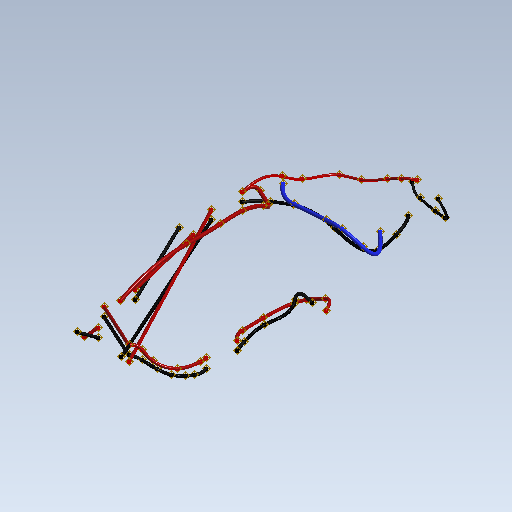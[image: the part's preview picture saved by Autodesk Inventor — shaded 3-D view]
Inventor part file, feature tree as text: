
AUTODESK INVENTOR PART (.ipt)
format: ipt  version: 2020.1 (Build 241239000, 239)  size: 1,614,336 bytes
history: native  units: mm (DEFAULTED — no unit token found)
features: other x136, plane x35, sketch x35, sweep x35
ambient origin geometry x8: Origin, YZ Plane, XZ Plane, XY Plane, X Axis, Y Axis, Z Axis, Center Point
bodies: Body1 (feature_tree), Body2 (feature_tree), Body3 (feature_tree), Body4 (feature_tree), Body5 (feature_tree), Body6 (feature_tree), Body7 (feature_tree), Body8 (feature_tree), Body9 (feature_tree), Body10 (feature_tree), Body11 (feature_tree), Body12 (feature_tree), Body13 (feature_tree), Body14 (feature_tree), Body15 (feature_tree), Body16 (feature_tree), Body17 (feature_tree), Body18 (feature_tree), Body19 (feature_tree), Body20 (feature_tree), Body21 (feature_tree), Body22 (feature_tree), Body23 (feature_tree), Body24 (feature_tree), Body25 (feature_tree), Body26 (feature_tree), Body27 (feature_tree), Body28 (feature_tree), Body29 (feature_tree), Body30 (feature_tree), Body31 (feature_tree), Body32 (feature_tree), Body33 (feature_tree), Body34 (feature_tree), Body35 (feature_tree)
feature tree (241):
  other  "Work Point1"
  other  "Work Point2"
  other  "P- / Switch>XT60"
  other  "Work Point3"
  other  "Work Point4"
  other  "P+ / Switch>XT60"
  other  "Work Point5"
  other  "Work Point6"
  other  "P- / XT60>XT60 VESC1"
  other  "Work Point7"
  other  "Work Point8"
  other  "P+ / XT60>XT60 VESC1"
  other  "Work Point9"
  other  "Work Point10"
  other  "P- / XT60>XT60 VESC2"
  other  "Work Point11"
  other  "Work Point12"
  other  "P+ / XT60>XT60 VESC2"
  other  "Work Point13"
  other  "Work Point14"
  other  "P- / XT60 VESC1>VESC1"
  other  "Work Point15"
  other  "Work Point16"
  other  "P+ / XT60 VESC1>VESC1"
  other  "Work Point17"
  other  "Work Point18"
  other  "P- / XT60 VESC2>VESC2"
  other  "Work Point19"
  other  "Work Point20"
  other  "P+ / XT60 VESC2>VESC2"
  other  "Work Point21"
  other  "Work Point22"
  other  "P- / XT60 B>Switch"
  other  "Work Point23"
  other  "Work Point24"
  other  "P+ / XT60 B>Switch"
  other  "Work Point25"
  other  "Work Point26"
  other  "B- / BAT>BMS"
  other  "Work Point27"
  other  "Work Point28"
  other  "B- / BMS>XT60 B"
  other  "Work Point29"
  other  "Work Point30"
  other  "B+ / BAT>XT60 B"
  other  "Work Point31"
  other  "Work Point32"
  other  "C- / XLR F>BMS"
  other  "Work Point33"
  other  "Work Point34"
  other  "C+ / XLR F>XT60 B"
  plane  "Work Plane9"
  plane  "Work Plane10"
  plane  "Work Plane11"
  plane  "Work Plane12"
  plane  "Work Plane43"
  plane  "Work Plane44"
  plane  "Work Plane47"
  other  "Work Point55"
  other  "Work Point56"
  other  "Segment1"
  other  "Work Point57"
  other  "Work Point58"
  other  "Work Point62"
  other  "Work Point63"
  other  "Segment2"
  other  "Work Point64"
  other  "Work Point65"
  other  "Work Point66"
  plane  "Work Plane54"
  plane  "Work Plane55"
  plane  "Work Plane56"
  other  "Work Point67"
  other  "Work Point68"
  other  "Segment3"
  other  "Work Point69"
  other  "Work Point70"
  plane  "Work Plane57"
  plane  "Work Plane58"
  plane  "Work Plane59"
  other  "Work Point71"
  other  "Work Point72"
  other  "Segment4"
  other  "Work Point73"
  other  "Work Point75"
  plane  "Work Plane62"
  plane  "Work Plane64"
  plane  "Work Plane65"
  other  "Work Point77"
  other  "Work Point78"
  other  "Segment5"
  other  "Work Point79"
  plane  "Work Plane66"
  plane  "Work Plane67"
  plane  "Work Plane68"
  other  "Work Point80"
  other  "Work Point81"
  other  "Segment6"
  other  "Work Point82"
  other  "Work Point83"
  other  "Work Point84"
  other  "Work Point85"
  plane  "Work Plane69"
  plane  "Work Plane70"
  plane  "Work Plane71"
  other  "Segment8"
  other  "Work Point95"
  other  "Work Point96"
  other  "Work Point97"
  other  "Work Point98"
  other  "Work Point99"
  other  "Work Point100"
  other  "Work Point101"
  other  "Work Point102"
  other  "Segment9"
  other  "Work Point103"
  other  "Work Point104"
  plane  "Work Plane79"
  plane  "Work Plane80"
  plane  "Work Plane81"
  other  "Work Point105"
  other  "Work Point106"
  other  "Segment10"
  other  "Work Point107"
  other  "Work Point108"
  other  "Work Point109"
  plane  "Work Plane82"
  plane  "Work Plane83"
  plane  "Work Plane84"
  plane  "Work Plane90"
  plane  "Work Plane91"
  plane  "Work Plane92"
  plane  "Work Plane93"
  plane  "Work Plane102"
  plane  "Work Plane103"
  plane  "Work Plane104"
  sketch  "Sketch9"  dims[d16=0.0mm d17=0.0mm d18=0.0mm d19=0.0mm]
  other  "Srf9"
  sketch  "Sketch10"  dims[d20=0.0mm d21=0.0mm d22=0.0mm d23=0.0mm]
  other  "Srf10"
  sketch  "Sketch11"  dims[d76=0.0mm d77=0.0mm d78=0.0mm d79=0.0mm]
  other  "Srf11"
  sketch  "Sketch12"  dims[d84=0.0mm d85=0.0mm d98=0.0mm d99=0.0mm]
  other  "Srf12"
  sketch  "Sketch43"  dims[d100=0.0mm d101=0.0mm d102=0.0mm d103=0.0mm]
  other  "Srf39"
  sketch  "Sketch44"  dims[d104=0.0mm d105=0.0mm d106=0.0mm d107=0.0mm]
  other  "Srf40"
  sketch  "Sketch47"  dims[d108=0.0mm d109=0.0mm d114=0.0mm d115=0.0mm]
  other  "Srf43"
  sketch  "Sketch54"  dims[d118=0.0mm d119=0.0mm d120=0.0mm d121=0.0mm]
  other  "Srf50"
  sketch  "Sketch55"  dims[d122=0.0mm d123=0.0mm d124=0.0mm d125=0.0mm]
  other  "Srf51"
  sketch  "Sketch56"  dims[d126=0.0mm d127=0.0mm d128=0.0mm d129=0.0mm]
  other  "Srf52"
  sketch  "Sketch57"  dims[d130=0.0mm d131=0.0mm d132=0.0mm d133=0.0mm]
  other  "Srf53"
  sketch  "Sketch58"  dims[d148=0.0mm d149=0.0mm d150=0.0mm d151=0.0mm]
  other  "Srf54"
  sketch  "Sketch59"  dims[d152=0.0mm d153=0.0mm d154=0.0mm d155=0.0mm]
  other  "Srf55"
  sketch  "Sketch62"  dims[d156=0.0mm d157=0.0mm d158=0.0mm d159=0.0mm]
  other  "Srf58"
  sketch  "Sketch64"  dims[d168=0.0mm d169=0.0mm d170=0.0mm d171=0.0mm]
  other  "Srf60"
  sketch  "Sketch65"  dims[d172=0.0mm d173=0.0mm d174=0.0mm d175=0.0mm]
  other  "Srf61"
  sketch  "Sketch66"  dims[d190=0.0mm d191=0.0mm d192=0.0mm d193=0.0mm]
  other  "Srf62"
  sketch  "Sketch67"  dims[d194=0.0mm d195=0.0mm]
  other  "Srf63"
  sketch  "Sketch68"
  other  "Srf64"
  sketch  "Sketch69"
  other  "Srf65"
  sketch  "Sketch70"
  other  "Srf66"
  sketch  "Sketch71"
  other  "Srf67"
  sketch  "Sketch79"
  other  "Srf75"
  sketch  "Sketch80"
  other  "Srf76"
  sketch  "Sketch81"
  other  "Srf77"
  sketch  "Sketch82"
  other  "Srf78"
  sketch  "Sketch83"
  other  "Srf79"
  sketch  "Sketch84"
  other  "Srf80"
  sketch  "Sketch90"
  other  "Srf85"
  sketch  "Sketch91"
  other  "Srf86"
  sketch  "Sketch92"
  other  "Srf87"
  sketch  "Sketch93"
  other  "Srf88"
  sketch  "Sketch102"
  other  "Srf96"
  sketch  "Sketch103"
  other  "Srf97"
  sketch  "Sketch104"
  other  "Srf98"
  sweep  "SweepSrf9"
  sweep  "SweepSrf10"
  sweep  "SweepSrf11"
  sweep  "SweepSrf12"
  sweep  "SweepSrf39"
  sweep  "SweepSrf40"
  sweep  "SweepSrf43"
  sweep  "SweepSrf50"
  sweep  "SweepSrf51"
  sweep  "SweepSrf52"
  sweep  "SweepSrf53"
  sweep  "SweepSrf54"
  sweep  "SweepSrf55"
  sweep  "SweepSrf58"
  sweep  "SweepSrf60"
  sweep  "SweepSrf61"
  sweep  "SweepSrf62"
  sweep  "SweepSrf63"
  sweep  "SweepSrf64"
  sweep  "SweepSrf65"
  sweep  "SweepSrf66"
  sweep  "SweepSrf67"
  sweep  "SweepSrf75"
  sweep  "SweepSrf76"
  sweep  "SweepSrf77"
  sweep  "SweepSrf78"
  sweep  "SweepSrf79"
  sweep  "SweepSrf80"
  sweep  "SweepSrf85"
  sweep  "SweepSrf86"
  sweep  "SweepSrf87"
  sweep  "SweepSrf88"
  sweep  "SweepSrf96"
  sweep  "SweepSrf97"
  sweep  "SweepSrf98"
